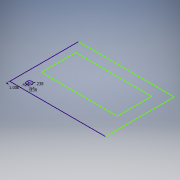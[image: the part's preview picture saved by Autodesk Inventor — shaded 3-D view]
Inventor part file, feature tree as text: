
AUTODESK INVENTOR PART (.ipt)
format: ipt  version: 2019 (Build 230136000, 136)  size: 94,208 bytes
history: native  units: in
note: dims shown in document units (in); Inventor stores cm internally (conversion verified against a paired STEP export)
features: sketch x1
ambient origin geometry x8: Origin, YZ Plane, XZ Plane, XY Plane, X Axis, Y Axis, Z Axis, Center Point
feature tree (1):
  sketch  "Sketch2"  dims[d0=0.4291in d1=0.4724in d2=0.2382in d3=0.2382in d4=0.75in d5=1.0in]
